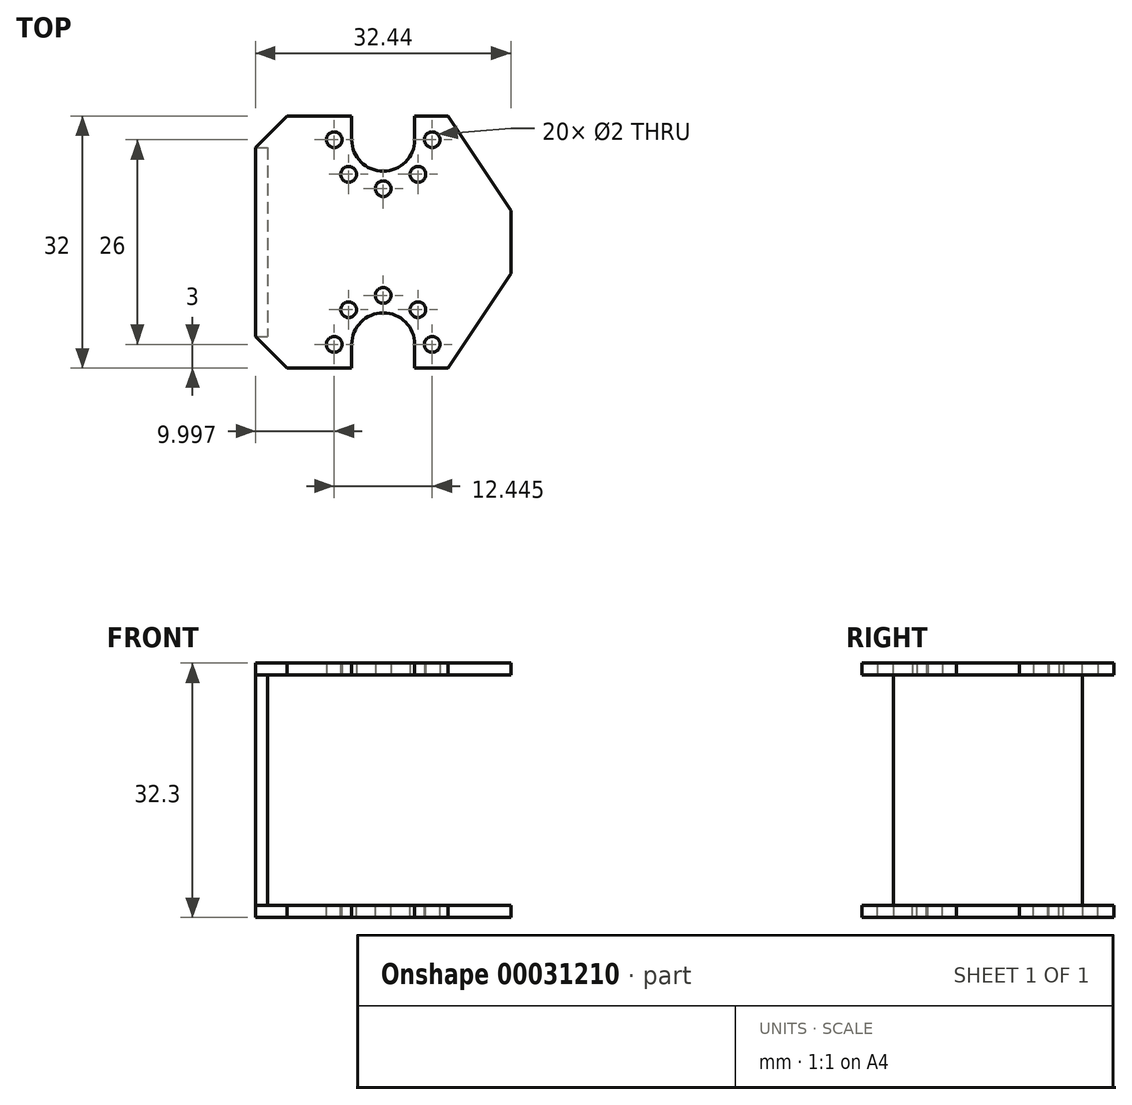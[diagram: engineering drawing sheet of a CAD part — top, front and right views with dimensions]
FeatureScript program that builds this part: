
annotation { "Feature Type Name" : "Feature", "Feature Type Description" : "" }
export const myFeature = defineFeature(function(context is Context, id is Id, definition is map)
    precondition{}
    {
        {
            var Q0;
            Q0=qCreatedBy(makeId("Top.planeOp"),FACE);
            var sketch = newSketch(context, id + "F0", { "sketchPlane" : qUnion([Q0])});
            skLineSegment(sketch, "E0.bottom", {"start": v(-16.22, 16) * mm, "end": v(-4, 16) * mm});
            skLineSegment(sketch, "E0.top", {"start": v(-16.22, -16) * mm, "end": v(-4, -16) * mm});
            skLineSegment(sketch, "E0.left", {"start": v(-16.22, 16) * mm, "end": v(-16.22, -16) * mm});
            skLineSegment(sketch, "E0.right", {"start": v(16.22, 16) * mm, "end": v(16.22, -16) * mm});
            skPoint(sketch, "E0.middle", {"position": v(0, 0) * mm});
            skArc(sketch, "E1", {"start": v(-4, 13) * mm, "mid": v(0, 9) * mm, "end": v(4, 13) * mm});
            skLineSegment(sketch, "E2.bottom", {"start": v(4.4, 8.6) * mm, "end": v(-4.4, 8.6) * mm, "construction": true});
            skLineSegment(sketch, "E2.top", {"start": v(4.4, 17.4) * mm, "end": v(-4.4, 17.4) * mm, "construction": true});
            skLineSegment(sketch, "E2.left", {"start": v(4.4, 8.6) * mm, "end": v(4.4, 17.4) * mm, "construction": true});
            skLineSegment(sketch, "E2.right", {"start": v(-4.4, 8.6) * mm, "end": v(-4.4, 17.4) * mm, "construction": true});
            skCircle(sketch, "E3", {"center": v(4.4, 8.6) * mm, "radius": 1 * mm});
            skCircle(sketch, "E4.1.0", {"center": v(6.22, 13) * mm, "radius": 1 * mm});
            skCircle(sketch, "E4.5.0", {"center": v(-6.22, 13) * mm, "radius": 1 * mm});
            skCircle(sketch, "E4.6.0", {"center": v(-4.4, 8.6) * mm, "radius": 1 * mm});
            skCircle(sketch, "E4.7.0", {"center": v(0, 6.78) * mm, "radius": 1 * mm});
            skLineSegment(sketch, "E5", {"start": v(-4, 13) * mm, "end": v(-4, 16) * mm});
            skLineSegment(sketch, "E6", {"start": v(4, 13) * mm, "end": v(4, 16) * mm});
            skLineSegment(sketch, "E7.trimOffspring", {"start": v(4, 16) * mm, "end": v(16.22, 16) * mm});
            skPoint(sketch, "E8.MirrorP", {"position": v(0, -13) * mm});
            skLineSegment(sketch, "E9.MirrorCS", {"start": v(-4, -13) * mm, "end": v(-4, -16) * mm});
            skCircle(sketch, "E10.MirrorC", {"center": v(0, -6.78) * mm, "radius": 1 * mm});
            skLineSegment(sketch, "E11.MirrorCS", {"start": v(4, -13) * mm, "end": v(4, -16) * mm});
            skCircle(sketch, "E12.MirrorC", {"center": v(-4.4, -8.6) * mm, "radius": 1 * mm});
            skCircle(sketch, "E13.MirrorC", {"center": v(6.22, -13) * mm, "radius": 1 * mm});
            skCircle(sketch, "E14.MirrorC", {"center": v(-6.22, -13) * mm, "radius": 1 * mm});
            skArc(sketch, "E15.MirrorCS", {"start": v(-4, -13) * mm, "mid": v(0, -9) * mm, "end": v(4, -13) * mm});
            skCircle(sketch, "E16.MirrorC", {"center": v(4.4, -8.6) * mm, "radius": 1 * mm});
            skLineSegment(sketch, "E17.trimOffspring", {"start": v(4, -16) * mm, "end": v(16.22, -16) * mm});
            skSolve(sketch);
        }
        {
            var Q0;
            Q0 = qSketchRegion(id + "F0", true);
            extrude(context, id + "F1", {"entities" : qUnion([Q0]), "depth" : 1.5 * mm});
        }
        {
            var Q0;
            Q0=makeQuery(id+"F1.opExtrude","CAP_FACE",FACE,{"disambiguationData":[OSD([sQuery(id+"F0.wireOp",EDGE,"E0.bottom"),sQuery(id+"F0.wireOp",EDGE,"E0.top"),sQuery(id+"F0.wireOp",EDGE,"E0.left"),sQuery(id+"F0.wireOp",EDGE,"E0.right"),sQuery(id+"F0.wireOp",EDGE,"E1"),sQuery(id+"F0.wireOp",EDGE,"E3"),sQuery(id+"F0.wireOp",EDGE,"E4.1.0"),sQuery(id+"F0.wireOp",EDGE,"E4.5.0"),sQuery(id+"F0.wireOp",EDGE,"E4.6.0"),sQuery(id+"F0.wireOp",EDGE,"E4.7.0"),sQuery(id+"F0.wireOp",EDGE,"E5"),sQuery(id+"F0.wireOp",EDGE,"E6"),sQuery(id+"F0.wireOp",EDGE,"E7.trimOffspring"),sQuery(id+"F0.wireOp",EDGE,"E9.MirrorCS"),sQuery(id+"F0.wireOp",EDGE,"E10.MirrorC"),sQuery(id+"F0.wireOp",EDGE,"E11.MirrorCS"),sQuery(id+"F0.wireOp",EDGE,"E12.MirrorC"),sQuery(id+"F0.wireOp",EDGE,"E13.MirrorC"),sQuery(id+"F0.wireOp",EDGE,"E14.MirrorC"),sQuery(id+"F0.wireOp",EDGE,"E15.MirrorCS"),sQuery(id+"F0.wireOp",EDGE,"E16.MirrorC"),sQuery(id+"F0.wireOp",EDGE,"E17.trimOffspring")])],"isStart":false});
            var sketch = newSketch(context, id + "F2", { "sketchPlane" : qUnion([Q0])});
            skPoint(sketch, "E18", {"position": v(6.22, 13) * mm});
            skPoint(sketch, "E19", {"position": v(6.22, -13) * mm});
            skLineSegment(sketch, "E20", {"start": v(8.22, 16) * mm, "end": v(16.22, 4) * mm});
            skLineSegment(sketch, "E21", {"start": v(16.22, 4) * mm, "end": v(16.22, 16) * mm});
            skLineSegment(sketch, "E22", {"start": v(16.22, 16) * mm, "end": v(8.22, 16) * mm});
            skLineSegment(sketch, "E23.MirrorCS", {"start": v(16.22, -16) * mm, "end": v(8.22, -16) * mm});
            skLineSegment(sketch, "E24.MirrorCS", {"start": v(16.22, -4) * mm, "end": v(16.22, -16) * mm});
            skLineSegment(sketch, "E25.MirrorCS", {"start": v(8.22, -16) * mm, "end": v(16.22, -4) * mm});
            skLineSegment(sketch, "E26", {"start": v(-16.22, 16) * mm, "end": v(-16.22, 12) * mm});
            skLineSegment(sketch, "E27", {"start": v(-16.22, 12) * mm, "end": v(-12.22, 16) * mm});
            skLineSegment(sketch, "E28", {"start": v(-12.22, 16) * mm, "end": v(-16.22, 16) * mm});
            skLineSegment(sketch, "E29.MirrorCS", {"start": v(-12.22, -16) * mm, "end": v(-16.22, -16) * mm});
            skLineSegment(sketch, "E30.MirrorCS", {"start": v(-16.22, -12) * mm, "end": v(-12.22, -16) * mm});
            skLineSegment(sketch, "E31.MirrorCS", {"start": v(-16.22, -16) * mm, "end": v(-16.22, -12) * mm});
            skSolve(sketch);
        }
        {
            var Q0;
            Q0 = qSketchRegion(id + "F2", true);
            extrude(context, id + "F3", {"entities" : qUnion([Q0]), "operationType" : NewBodyOperationType.REMOVE, "endBound" : BoundingType.UP_TO_NEXT, "oppositeDirection" : true, "depth" : 25 * mm});
        }
        {
            var Q0;
            Q0=makeQuery(id+"F1.opExtrude","CAP_FACE",FACE,{"disambiguationData":[OSD([sQuery(id+"F0.wireOp",EDGE,"E0.bottom"),sQuery(id+"F0.wireOp",EDGE,"E0.top"),sQuery(id+"F0.wireOp",EDGE,"E0.left"),sQuery(id+"F0.wireOp",EDGE,"E0.right"),sQuery(id+"F0.wireOp",EDGE,"E1"),sQuery(id+"F0.wireOp",EDGE,"E3"),sQuery(id+"F0.wireOp",EDGE,"E4.1.0"),sQuery(id+"F0.wireOp",EDGE,"E4.5.0"),sQuery(id+"F0.wireOp",EDGE,"E4.6.0"),sQuery(id+"F0.wireOp",EDGE,"E4.7.0"),sQuery(id+"F0.wireOp",EDGE,"E5"),sQuery(id+"F0.wireOp",EDGE,"E6"),sQuery(id+"F0.wireOp",EDGE,"E7.trimOffspring"),sQuery(id+"F0.wireOp",EDGE,"E9.MirrorCS"),sQuery(id+"F0.wireOp",EDGE,"E10.MirrorC"),sQuery(id+"F0.wireOp",EDGE,"E11.MirrorCS"),sQuery(id+"F0.wireOp",EDGE,"E12.MirrorC"),sQuery(id+"F0.wireOp",EDGE,"E13.MirrorC"),sQuery(id+"F0.wireOp",EDGE,"E14.MirrorC"),sQuery(id+"F0.wireOp",EDGE,"E15.MirrorCS"),sQuery(id+"F0.wireOp",EDGE,"E16.MirrorC"),sQuery(id+"F0.wireOp",EDGE,"E17.trimOffspring")])],"isStart":true});
            var sketch = newSketch(context, id + "F4", { "sketchPlane" : qUnion([Q0])});
            skLineSegment(sketch, "E32.bottom", {"start": v(-16.22, -12) * mm, "end": v(-14.72, -12) * mm});
            skLineSegment(sketch, "E32.top", {"start": v(-16.22, 12) * mm, "end": v(-14.72, 12) * mm});
            skLineSegment(sketch, "E32.left", {"start": v(-16.22, -12) * mm, "end": v(-16.22, 12) * mm});
            skLineSegment(sketch, "E32.right", {"start": v(-14.72, -12) * mm, "end": v(-14.72, 12) * mm});
            skSolve(sketch);
        }
        {
            var Q0;
            Q0 = qSketchRegion(id + "F4", true);
            extrude(context, id + "F5", {"entities" : qUnion([Q0]), "operationType" : NewBodyOperationType.ADD, "depth" : (29.3 / 2) * mm});
        }
        {
            var Q0;
            Q0=qCreatedBy(makeId("Top.planeOp"),FACE);
            cPlane(context, id + "F6", {"entities" : qUnion([Q0]), "cplaneType" : CPlaneType.OFFSET, "offset" : (29.3 / 2) * mm, "oppositeDirection" : true, "width" : 150 * mm, "height" : 150 * mm});
        }
        {
            var Q0;
            Q0=makeQuery(id+"F1.opExtrude","SWEPT_BODY",BODY,{"disambiguationData":[OSD([sQuery(id+"F0.wireOp",EDGE,"E0.bottom"),sQuery(id+"F0.wireOp",EDGE,"E0.top"),sQuery(id+"F0.wireOp",EDGE,"E0.left"),sQuery(id+"F0.wireOp",EDGE,"E0.right"),sQuery(id+"F0.wireOp",EDGE,"E1"),sQuery(id+"F0.wireOp",EDGE,"E3"),sQuery(id+"F0.wireOp",EDGE,"E4.1.0"),sQuery(id+"F0.wireOp",EDGE,"E4.5.0"),sQuery(id+"F0.wireOp",EDGE,"E4.6.0"),sQuery(id+"F0.wireOp",EDGE,"E4.7.0"),sQuery(id+"F0.wireOp",EDGE,"E5"),sQuery(id+"F0.wireOp",EDGE,"E6"),sQuery(id+"F0.wireOp",EDGE,"E7.trimOffspring"),sQuery(id+"F0.wireOp",EDGE,"E9.MirrorCS"),sQuery(id+"F0.wireOp",EDGE,"E10.MirrorC"),sQuery(id+"F0.wireOp",EDGE,"E11.MirrorCS"),sQuery(id+"F0.wireOp",EDGE,"E12.MirrorC"),sQuery(id+"F0.wireOp",EDGE,"E13.MirrorC"),sQuery(id+"F0.wireOp",EDGE,"E14.MirrorC"),sQuery(id+"F0.wireOp",EDGE,"E15.MirrorCS"),sQuery(id+"F0.wireOp",EDGE,"E16.MirrorC"),sQuery(id+"F0.wireOp",EDGE,"E17.trimOffspring")])]});
            var Q1;
            Q1=qCreatedBy(id+"F6.planeOp",FACE);
            mirror(context, id + "F7", {"operationType" : NewBodyOperationType.ADD, "entities" : qUnion([Q0]), "mirrorPlane" : qUnion([Q1])});
        }
    });
